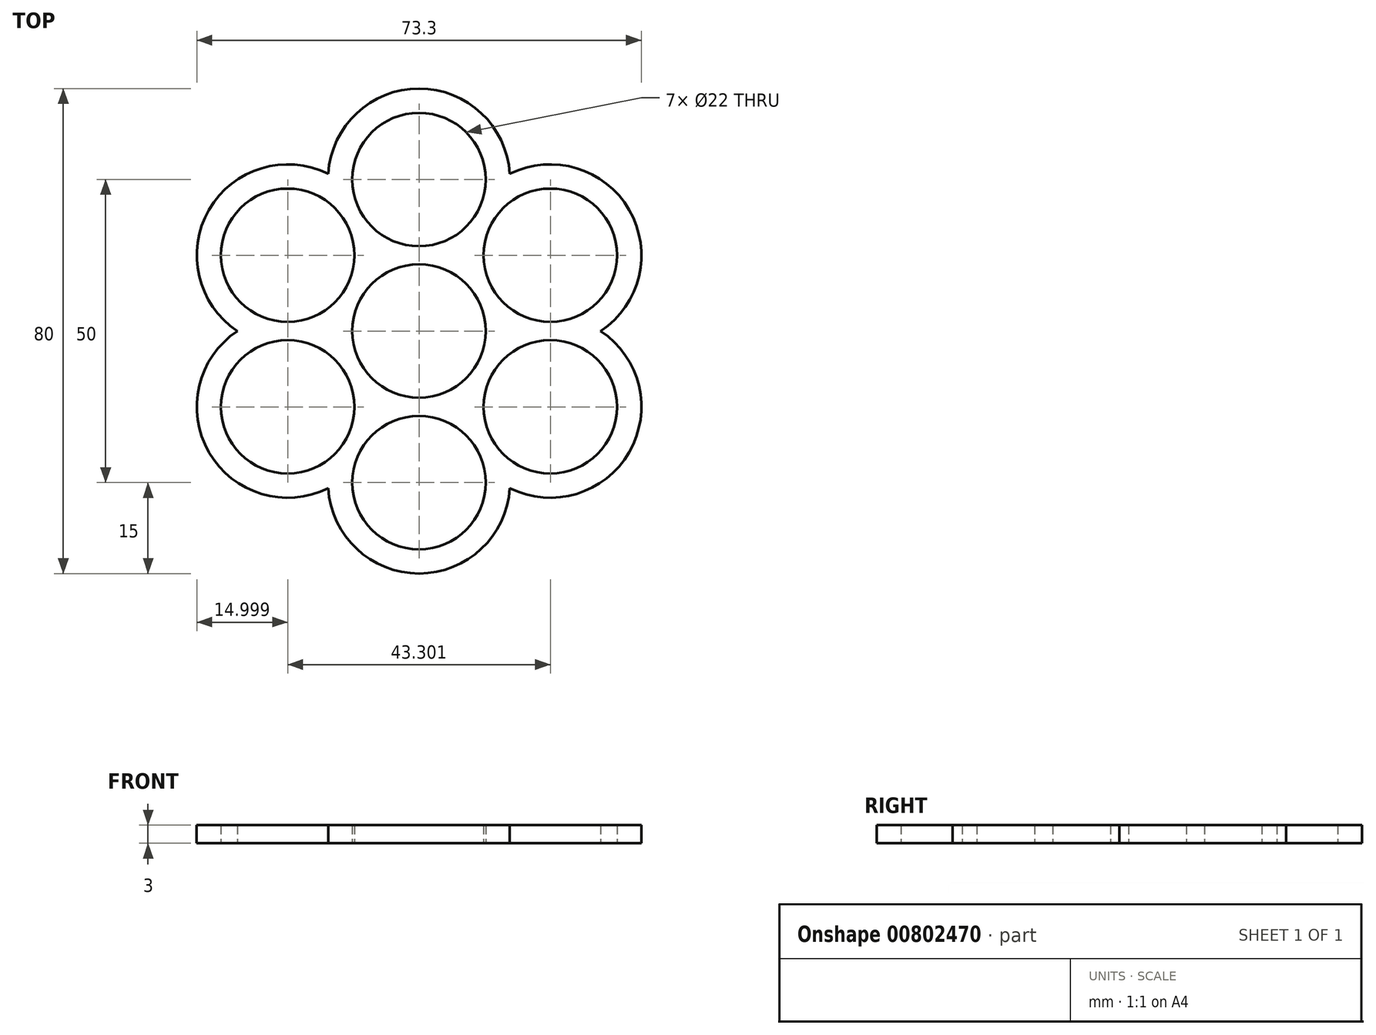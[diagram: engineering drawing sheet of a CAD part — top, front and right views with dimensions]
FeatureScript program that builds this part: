
annotation { "Feature Type Name" : "Feature", "Feature Type Description" : "" }
export const myFeature = defineFeature(function(context is Context, id is Id, definition is map)
    precondition{}
    {
        {
            var Q0;
            Q0=qCreatedBy(makeId("Top.planeOp"),FACE);
            var sketch = newSketch(context, id + "F0", { "sketchPlane" : qUnion([Q0])});
            skArc(sketch, "E0", {"start": v(5.5, 9.53) * mm, "mid": v(0, 11) * mm, "end": v(-5.5, 9.53) * mm});
            skCircle(sketch, "E1", {"center": v(0, 25) * mm, "radius": 11 * mm});
            skArc(sketch, "E2", {"start": v(14.97, 25.93) * mm, "mid": v(0, 40) * mm, "end": v(-14.97, 25.93) * mm});
            skArc(sketch, "E3.1.0", {"start": v(-14.97, 25.93) * mm, "mid": v(-34.64, 20) * mm, "end": v(-29.94, 0) * mm});
            skCircle(sketch, "E3.1.1", {"center": v(-21.65, 12.5) * mm, "radius": 11 * mm});
            skArc(sketch, "E3.1.2", {"start": v(-5.5, 9.53) * mm, "mid": v(-9.53, 5.5) * mm, "end": v(-11, 0) * mm});
            skArc(sketch, "E3.2.0", {"start": v(-29.94, 0) * mm, "mid": v(-34.64, -20) * mm, "end": v(-14.97, -25.93) * mm});
            skCircle(sketch, "E3.2.1", {"center": v(-21.65, -12.5) * mm, "radius": 11 * mm});
            skArc(sketch, "E3.2.2", {"start": v(-11, 0) * mm, "mid": v(-9.53, -5.5) * mm, "end": v(-5.5, -9.53) * mm});
            skArc(sketch, "E3.3.0", {"start": v(-14.97, -25.93) * mm, "mid": v(0, -40) * mm, "end": v(14.97, -25.93) * mm});
            skCircle(sketch, "E3.3.1", {"center": v(0, -25) * mm, "radius": 11 * mm});
            skArc(sketch, "E3.3.2", {"start": v(-5.5, -9.53) * mm, "mid": v(0, -11) * mm, "end": v(5.5, -9.53) * mm});
            skArc(sketch, "E3.4.0", {"start": v(14.97, -25.93) * mm, "mid": v(34.64, -20) * mm, "end": v(29.94, 0) * mm});
            skCircle(sketch, "E3.4.1", {"center": v(21.65, -12.5) * mm, "radius": 11 * mm});
            skArc(sketch, "E3.4.2", {"start": v(5.5, -9.53) * mm, "mid": v(9.53, -5.5) * mm, "end": v(11, 0) * mm});
            skArc(sketch, "E3.5.0", {"start": v(29.94, 0) * mm, "mid": v(34.64, 20) * mm, "end": v(14.97, 25.93) * mm});
            skCircle(sketch, "E3.5.1", {"center": v(21.65, 12.5) * mm, "radius": 11 * mm});
            skArc(sketch, "E3.5.2", {"start": v(11, 0) * mm, "mid": v(9.53, 5.5) * mm, "end": v(5.5, 9.53) * mm});
            skSolve(sketch);
        }
        {
            var Q0;
            Q0 = qSketchRegion(id + "F0", true);
            extrude(context, id + "F1", {"entities" : qUnion([Q0]), "depth" : 3 * mm, "offsetDistance" : 25 * mm});
        }
    });
